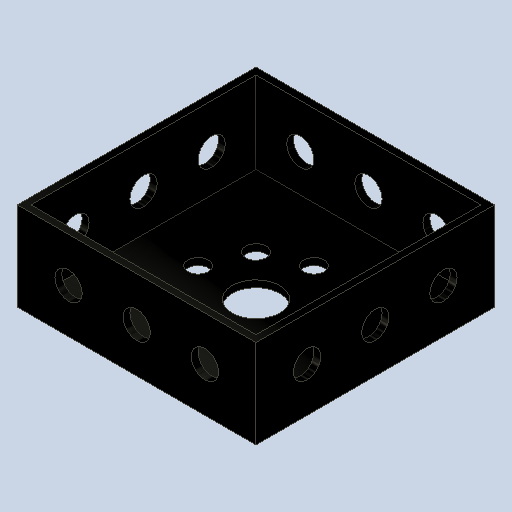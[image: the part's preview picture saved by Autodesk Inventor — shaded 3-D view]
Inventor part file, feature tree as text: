
AUTODESK INVENTOR PART (.ipt)
format: ipt  version: 2022 (Build 260153000, 153)  size: 214,016 bytes
history: native  units: mm
features: extrude x4, sketch x4, other x1, projected_geometry x1
ambient origin geometry x8: Origin, YZ Plane, XZ Plane, XY Plane, X Axis, Y Axis, Z Axis, Center Point
bodies: Body1 (feature_tree)
feature tree (10):
  other  "Твердое тело1"
  extrude  "Выдавливание1"  Depth=7.0mm
  extrude  "Выдавливание2"  Depth=3.0mm
  extrude  "Выдавливание3"  Depth=8.5mm
  extrude  "Выдавливание4"  Depth=80.0mm TaperAngle=360.0deg
  sketch  "Эскиз1"
  sketch  "Эскиз2"
  projected_geometry  "Спроецированная петля1"
  sketch  "Эскиз3"
  sketch  "Эскиз4"
